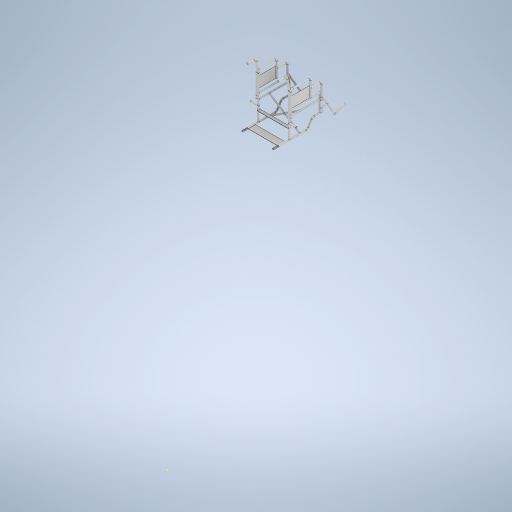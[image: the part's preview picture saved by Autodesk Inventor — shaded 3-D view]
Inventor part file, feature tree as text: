
AUTODESK INVENTOR PART (.ipt)
format: ipt  version: 2023 (Build 270158000, 158)  size: 630,272 bytes
history: native  units: in
note: dims shown in document units (in); Inventor stores cm internally (conversion verified against a paired STEP export)
features: sketch x29, plane x19, sweep x12, extrude x12, mirror x3
ambient origin geometry x8: Origin, YZ Plane, XZ Plane, XY Plane, X Axis, Y Axis, Z Axis, Center Point
bodies: Solid1 (feature_tree)
feature tree (75):
  sketch  "Sketch1"  dims[d14=3.5in d15=1.5in]
  plane  "Work Plane1"
  sweep  "Sweep1"
  sweep  "Sweep2"
  sweep  "Sweep3"
  sketch  "Sketch5"  dims[d22=17.0in d23=6.0in]
  plane  "Work Plane2"
  sweep  "Sweep4"
  plane  "Work Plane3"
  sweep  "Sweep5"
  plane  "Work Plane4"
  sweep  "Sweep6"
  sweep  "Sweep7"
  plane  "Work Plane5"
  sweep  "Sweep8"
  extrude  "Extrusion1"  Depth=9.8677in
  plane  "Work Plane6"
  sketch  "Sketch11"  dims[d37=0.0in d38=0.0in d39=0.0in d40=0.0in]
  plane  "Work Plane7"
  sketch  "Sketch12"  dims[d41=0.875in d42=0.0in d43=0.0in]
  plane  "Work Plane8"
  sweep  "Sweep9"
  sweep  "Sweep10"
  plane  "Work Plane9"
  extrude  "Extrusion2"  TaperAngle=0.0deg  [1 undecoded]
  plane  "Work Plane10"
  mirror  "Mirror1"
  sketch  "Sketch18"  dims[d50=0.875in d51=0.0in d52=0.0in]
  extrude  "Extrusion4"  TaperAngle=0.0deg  [1 undecoded]
  extrude  "Extrusion5"  TaperAngle=0.0deg  [1 undecoded]
  plane  "Work Plane13"
  mirror  "Mirror2"
  plane  "Work Plane14"
  extrude  "Extrusion6"  TaperAngle=0.0deg  [1 undecoded]
  extrude  "Extrusion7"  TaperAngle=0.0deg  [1 undecoded]
  sketch  "Sketch23"  dims[d63=17.0in d64=0.875in]
  plane  "Work Plane15"
  sketch  "Sketch24"  dims[d65=0.875in d66=0.0in d67=0.0in]
  sweep  "Sweep11"
  plane  "Work Plane16"
  sketch  "Sketch25"  dims[d68=0.0in d69=0.0in d70=0.875in]
  sketch  "Sketch26"  dims[d71=0.875in d72=0.75in]
  sweep  "Sweep12"
  extrude  "Extrusion8"  Depth=11.0in
  mirror  "Mirror3"
  plane  "Work Plane17"
  extrude  "Extrusion9"  Depth=0.875in
  plane  "Work Plane18"
  extrude  "Extrusion10"  TaperAngle=0.0deg  [1 undecoded]
  plane  "Work Plane19"
  extrude  "Extrusion11"  Depth=0.875in
  plane  "Work Plane20"
  sketch  "Sketch31"  dims[d92=0.75in]
  plane  "Work Plane21"
  extrude  "Extrusion12"  Depth=0.75in
  extrude  "Extrusion13"  Depth=2.8125in TaperAngle=0.0deg
  sketch  "Sketch2"  dims[d16=6.0in d17=3.0in]
  sketch  "Sketch3"  dims[d18=30.0deg d19=0.6871in]
  sketch  "Sketch4"  dims[d20=6.0in d21=16.0in]
  sketch  "Sketch6"  dims[d24=17.0in d25=9.5in]
  sketch  "Sketch7"  dims[d26=10.0in d28=1.5in]
  sketch  "Sketch8"  dims[d29=1.5in d30=3.0in]
  sketch  "Sketch9"  dims[d31=31.0in d33=9.8677in]
  sketch  "Sketch10"  dims[d34=0.875in d35=0.0in d36=0.0in]
  sketch  "Sketch13"  dims[d44=0.875in d45=0.0in d46=0.0in]
  sketch  "Sketch14"  dims[d47=0.875in d48=0.0in d49=0.0in]
  sketch  "Sketch19"  dims[d53=0.875in d54=0.0in d55=0.0in]
  sketch  "Sketch20"  dims[d56=0.75in d57=0.875in]
  sketch  "Sketch21"  dims[d58=8.0in d59=4.0in d60=0.0in]
  sketch  "Sketch22"  dims[d61=-12.0in d62=11.0in]
  sketch  "Sketch27"  dims[d73=2.0in d74=0.0in d86=2.8125in d87=0.0in]
  sketch  "Sketch28"  dims[d88=0.5in]
  sketch  "Sketch29"  dims[d89=4.5in d90=0.0in]
  sketch  "Sketch30"  dims[d91=0.875in]
  sketch  "Sketch32"  dims[d93=0.875in d94=0.75in d95=1.5in d96=0.0in d97=0.875in d98=0.75in d99=1.5in d100=0.0in d102=12.0in d103=1.0in d104=11.0in d105=4.75in d106=4.5in d107=0.0in d108=0.0in d109=0.0in d110=0.0in d111=6.0in d112=0.0in d113=0.02in d114=0.0in d115=5.105in d116=0.0in d117=9.5825in d118=0.0in d119=0.0591in d120=3.937in d121=0.0591in d122=3.937in d123=16.4562in d124=0.0in d125=2.0282in d126=0.7874in d127=90.0deg d128=0.7874in d129=16.125in d130=0.0in d131=90.0deg d132=90.0deg d133=90.0deg d134=90.0deg d135=16.125in d136=0.0in d81=0.0197in d82=0.0344in d83=0.0197in d84=0.0344in]
note: 6 required parameter values undecoded (feature->parameter linkage not recoverable at this tier; creation-order binding heuristic only, values carry confidence <= 0.55)
